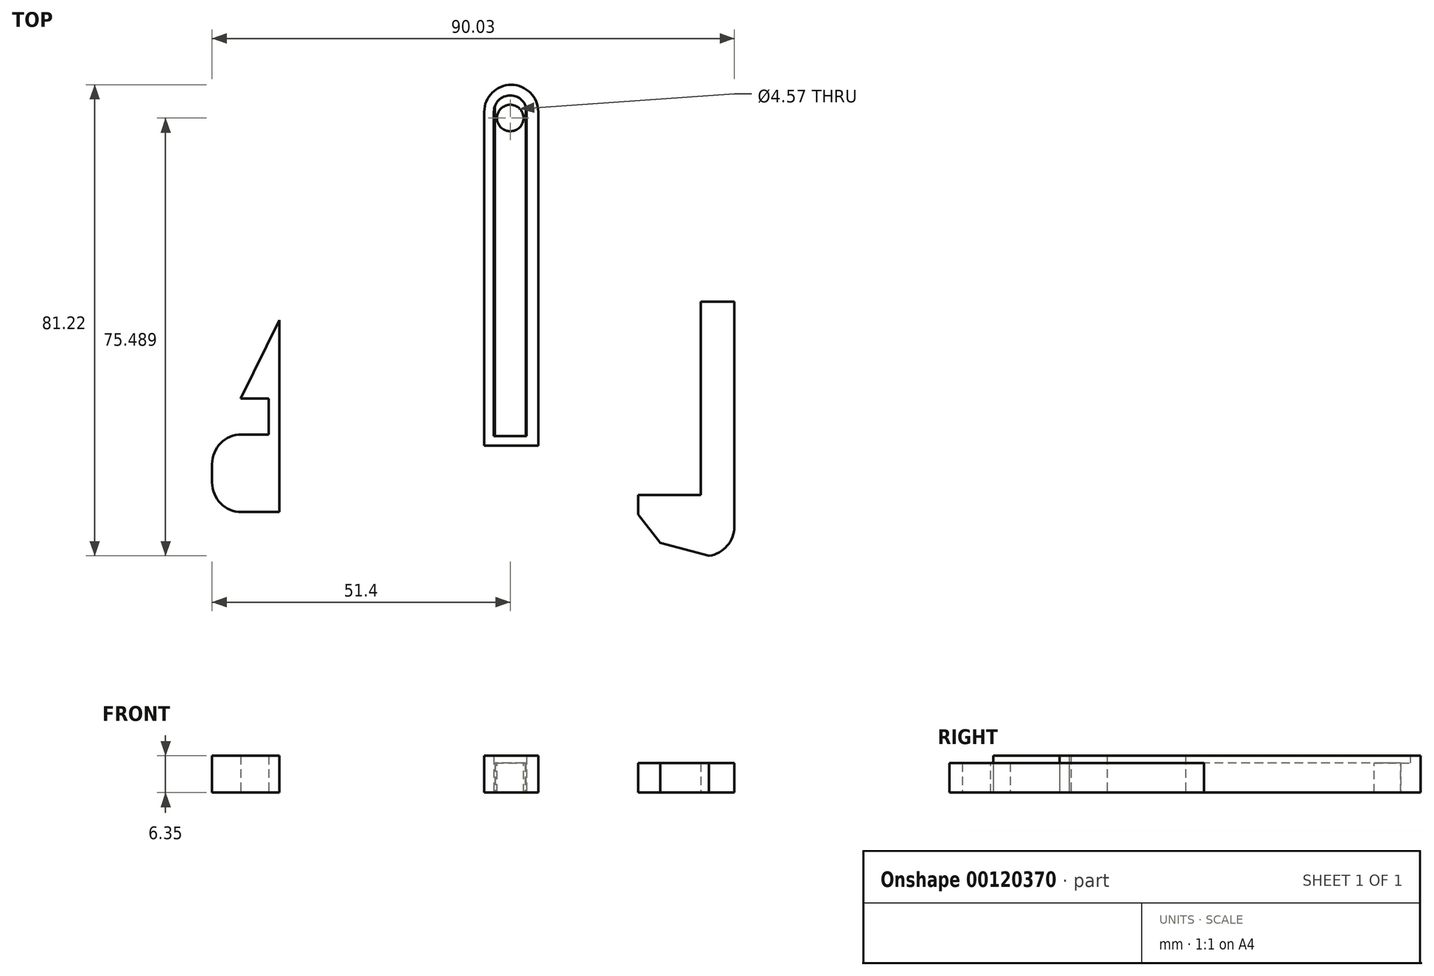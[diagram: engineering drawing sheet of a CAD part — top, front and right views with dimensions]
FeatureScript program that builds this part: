
annotation { "Feature Type Name" : "Feature", "Feature Type Description" : "" }
export const myFeature = defineFeature(function(context is Context, id is Id, definition is map)
    precondition{}
    {
        {
            var Q0;
            Q0=qCreatedBy(makeId("Top.planeOp"),FACE);
            var sketch = newSketch(context, id + "F0", { "sketchPlane" : qUnion([Q0])});
            skLineSegment(sketch, "E0.bottom", {"start": v(-2.66, 49.92) * mm, "end": v(2.66, 49.92) * mm});
            skLineSegment(sketch, "E0.top", {"start": v(-2.66, -6.85) * mm, "end": v(2.66, -6.85) * mm});
            skLineSegment(sketch, "E0.left", {"start": v(-2.66, 49.92) * mm, "end": v(-2.66, -6.85) * mm});
            skLineSegment(sketch, "E0.right", {"start": v(2.66, 49.92) * mm, "end": v(2.66, -6.85) * mm});
            skPoint(sketch, "E0.middle", {"position": v(0, 21.53) * mm});
            skArc(sketch, "E1", {"start": v(2.66, 49.92) * mm, "mid": v(0, 52.58) * mm, "end": v(-2.66, 49.92) * mm});
            skSolve(sketch);
        }
        {
            var Q0;
            Q0 = qSketchRegion(id + "F0", true);
            extrude(context, id + "F1", {"entities" : qUnion([Q0]), "depth" : 5.08 * mm});
        }
        {
            var Q0;
            Q0=qCreatedBy(makeId("Top.planeOp"),FACE);
            var sketch = newSketch(context, id + "F2", { "sketchPlane" : qUnion([Q0])});
            skLineSegment(sketch, "E2", {"start": v(-2.82, -6.52) * mm, "end": v(-2.82, 49.42) * mm});
            skLineSegment(sketch, "E3", {"start": v(-2.82, 49.42) * mm, "end": v(-4.48, 49.42) * mm});
            skLineSegment(sketch, "E4", {"start": v(-4.48, 49.42) * mm, "end": v(-4.48, -8.18) * mm});
            skLineSegment(sketch, "E5", {"start": v(-4.48, -8.18) * mm, "end": v(4.81, -8.18) * mm});
            skLineSegment(sketch, "E6", {"start": v(4.81, -8.18) * mm, "end": v(4.81, 49.42) * mm});
            skLineSegment(sketch, "E7", {"start": v(4.81, 49.42) * mm, "end": v(2.82, 49.42) * mm});
            skLineSegment(sketch, "E8", {"start": v(2.82, 49.42) * mm, "end": v(2.82, -6.52) * mm});
            skLineSegment(sketch, "E9", {"start": v(2.82, -6.52) * mm, "end": v(-2.82, -6.52) * mm});
            skArc(sketch, "E10", {"start": v(2.82, 49.42) * mm, "mid": v(0, 52.24) * mm, "end": v(-2.82, 49.42) * mm});
            skArc(sketch, "E11", {"start": v(4.81, 49.42) * mm, "mid": v(0.17, 54.07) * mm, "end": v(-4.48, 49.42) * mm});
            skSolve(sketch);
        }
        {
            var Q0;
            Q0 = qSketchRegion(id + "F2", true);
            extrude(context, id + "F3", {"entities" : qUnion([Q0]), "operationType" : NewBodyOperationType.ADD, "depth" : 6.35 * mm});
        }
        {
            var Q0;
            Q0=qCreatedBy(makeId("Top.planeOp"),FACE);
            var sketch = newSketch(context, id + "F4", { "sketchPlane" : qUnion([Q0])});
            skLineSegment(sketch, "E12", {"start": v(-39.79, 13.5) * mm, "end": v(-39.79, 0) * mm});
            skLineSegment(sketch, "E13", {"start": v(-39.79, -6.24) * mm, "end": v(-39.79, -13.21) * mm});
            skLineSegment(sketch, "E14", {"start": v(-39.79, -13.21) * mm, "end": v(-39.79, -19.6) * mm});
            skPoint(sketch, "E14.endSnap0", {"position": v(-39.79, -9.73) * mm});
            skLineSegment(sketch, "E15", {"start": v(-39.79, 13.5) * mm, "end": v(-46.47, 0) * mm});
            skLineSegment(sketch, "E16", {"start": v(-46.47, 0) * mm, "end": v(-39.79, 0) * mm});
            skLineSegment(sketch, "E17", {"start": v(-39.79, -19.6) * mm, "end": v(-51.4, -19.6) * mm});
            skLineSegment(sketch, "E18", {"start": v(-51.4, -19.6) * mm, "end": v(-51.4, -6.24) * mm});
            skLineSegment(sketch, "E19", {"start": v(-51.4, -6.24) * mm, "end": v(-39.79, -6.24) * mm});
            skLineSegment(sketch, "E20", {"start": v(-39.79, -6.24) * mm, "end": v(-39.79, 0) * mm});
            skPoint(sketch, "E21.endSnap0", {"position": v(-35.29, -6.24) * mm});
            skLineSegment(sketch, "E22", {"start": v(-41.66, -6.24) * mm, "end": v(-41.66, 0) * mm});
            skSolve(sketch);
        }
        {
            var Q0;
            Q0 = qSketchRegion(id + "F4", true);
            extrude(context, id + "F5", {"entities" : qUnion([Q0]), "depth" : 6.35 * mm});
        }
        {
            var Q0;
            Q0=makeQuery(id+"F5.opExtrude","SWEPT_EDGE",EDGE,{"disambiguationData":[OSD([sQuery(id+"F4.wireOp",EDGE,"E18"),sQuery(id+"F4.wireOp",EDGE,"E19")])]});
            var Q1;
            Q1=makeQuery(id+"F5.opExtrude","SWEPT_EDGE",EDGE,{"disambiguationData":[OSD([sQuery(id+"F4.wireOp",EDGE,"E17"),sQuery(id+"F4.wireOp",EDGE,"E18")])]});
            fillet(context, id + "F6", {"entities" : qUnion([Q0, Q1]), "radius" : 5.08 * mm, "tangentPropagation" : true, "allowEdgeOverflow" : false});
        }
        {
            var Q0;
            Q0=qCreatedBy(makeId("Top.planeOp"),FACE);
            var sketch = newSketch(context, id + "F7", { "sketchPlane" : qUnion([Q0])});
            skLineSegment(sketch, "E23.bottom", {"start": v(32.82, 16.7) * mm, "end": v(38.63, 16.7) * mm});
            skLineSegment(sketch, "E23.top", {"start": v(32.82, -16.7) * mm, "end": v(38.63, -16.7) * mm});
            skLineSegment(sketch, "E23.left", {"start": v(32.82, 16.7) * mm, "end": v(32.82, -16.7) * mm});
            skLineSegment(sketch, "E23.right", {"start": v(38.63, 16.7) * mm, "end": v(38.63, -16.7) * mm});
            skPoint(sketch, "E23.middle", {"position": v(35.72, 0) * mm});
            skLineSegment(sketch, "E24", {"start": v(32.82, -16.7) * mm, "end": v(22.07, -16.7) * mm});
            skLineSegment(sketch, "E25", {"start": v(22.07, -16.7) * mm, "end": v(22.07, -23.96) * mm});
            skLineSegment(sketch, "E26", {"start": v(22.07, -23.96) * mm, "end": v(34.27, -27.15) * mm});
            skLineSegment(sketch, "E27", {"start": v(34.27, -27.15) * mm, "end": v(38.63, -27.15) * mm});
            skLineSegment(sketch, "E28", {"start": v(38.63, -27.15) * mm, "end": v(38.63, -16.7) * mm});
            skSolve(sketch);
        }
        {
            var Q0;
            Q0 = qSketchRegion(id + "F7", true);
            extrude(context, id + "F8", {"entities" : qUnion([Q0]), "depth" : 5.08 * mm});
        }
        {
            var Q0;
            Q0=makeQuery(id+"F8.opExtrude","SWEPT_EDGE",EDGE,{"disambiguationData":[OSD([sQuery(id+"F7.wireOp",EDGE,"E27"),sQuery(id+"F7.wireOp",EDGE,"E28")])]});
            fillet(context, id + "F9", {"entities" : qUnion([Q0]), "radius" : 5.08 * mm, "tangentPropagation" : true, "allowEdgeOverflow" : false});
        }
        {
            var Q0;
            Q0=makeQuery(id+"F8.opExtrude","SWEPT_EDGE",EDGE,{"disambiguationData":[OSD([sQuery(id+"F7.wireOp",EDGE,"E25"),sQuery(id+"F7.wireOp",EDGE,"E26")])]});
            chamfer(context, id + "F10", {"entities" : qUnion([Q0]), "width" : 5.08 * mm, "tangentPropagation" : true});
        }
        {
            var Q0;
            Q0=makeQuery(id+"F1.opExtrude","CAP_FACE",FACE,{"disambiguationData":[OSD([sQuery(id+"F0.wireOp",EDGE,"E0.top"),sQuery(id+"F0.wireOp",EDGE,"E0.left"),sQuery(id+"F0.wireOp",EDGE,"E0.right"),sQuery(id+"F0.wireOp",EDGE,"E1")])],"isStart":false});
            var sketch = newSketch(context, id + "F11", { "sketchPlane" : qUnion([Q0])});
            skCircle(sketch, "E29", {"center": v(0, 48.34) * mm, "radius": 1.95 * mm});
            skSolve(sketch);
        }
        {
            var Q0;
            Q0=sQuery(id+"F11.wireOp",VERTEX,"E29.center");
            var Q1;
            Q1=makeQuery(id+"F1.opExtrude","SWEPT_BODY",BODY,{"disambiguationData":[OSD([sQuery(id+"F0.wireOp",EDGE,"E0.top"),sQuery(id+"F0.wireOp",EDGE,"E0.left"),sQuery(id+"F0.wireOp",EDGE,"E0.right"),sQuery(id+"F0.wireOp",EDGE,"E1")])]});
            hole(context, id + "F12", {"style" : HoleStyle.SIMPLE, "endStyle" : HoleEndStyle.THROUGH, "holeDiameter" : 4.57 * mm, "locations" : qUnion([Q0]), "scope" : qUnion([Q1]), "isTappedThrough" : true});
        }
    });
